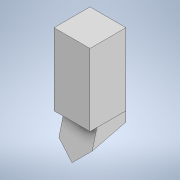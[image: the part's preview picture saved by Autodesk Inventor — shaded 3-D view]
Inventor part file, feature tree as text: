
AUTODESK INVENTOR PART (.ipt)
format: ipt  version: 2020 (Build 240168000, 168)  size: 161,792 bytes
history: native  units: mm
features: sketch x8, extrude x4, plane x4, other x4
ambient origin geometry x8: Origin, YZ Plane, XZ Plane, XY Plane, X Axis, Y Axis, Z Axis, Center Point
bodies: 实体1 (feature_tree), 实体2 (feature_tree), 实体3 (feature_tree)
feature tree (20):
  extrude  "拉伸1"  Depth=30.0mm
  sketch  "草图2"  dims[d2=10.0mm d3=10.0mm d4=0.0mm]
  plane  "工作平面4"
  other  "分割1"
  other  "三维草图1"
  sketch  "草图4"  dims[d5=45.0deg d6=150.0deg]
  extrude  "拉伸2"  Depth=10.0mm TaperAngle=0.0deg
  other  "正交平面2"
  sketch  "草图6"  dims[d10=90.0deg]
  sketch  "草图7"  dims[d11=75.0deg]
  plane  "工作平面3"
  extrude  "拉伸3"  TaperAngle=150.0deg  [1 undecoded]
  plane  "工作平面5"
  plane  "工作平面6"
  extrude  "拉伸4"  Depth=30.0mm TaperAngle=0.0deg
  sketch  "草图1"  dims[d0=5.0mm d1=30.0mm]
  sketch  "草图5"  dims[d7=30.543262mm d8=30.0mm d9=0.0mm]
  other  "正交平面"
  sketch  "草图8"  dims[d12=-20.0mm]
  sketch  "草图9"  dims[d13=15.0mm d14=15.0mm d15=20.0mm d16=30.0mm d17=0.0mm d18=1.745329mm d19=10.0mm d20=0.0mm]
note: 1 required parameter value undecoded (feature->parameter linkage not recoverable at this tier; creation-order binding heuristic only, values carry confidence <= 0.55)
